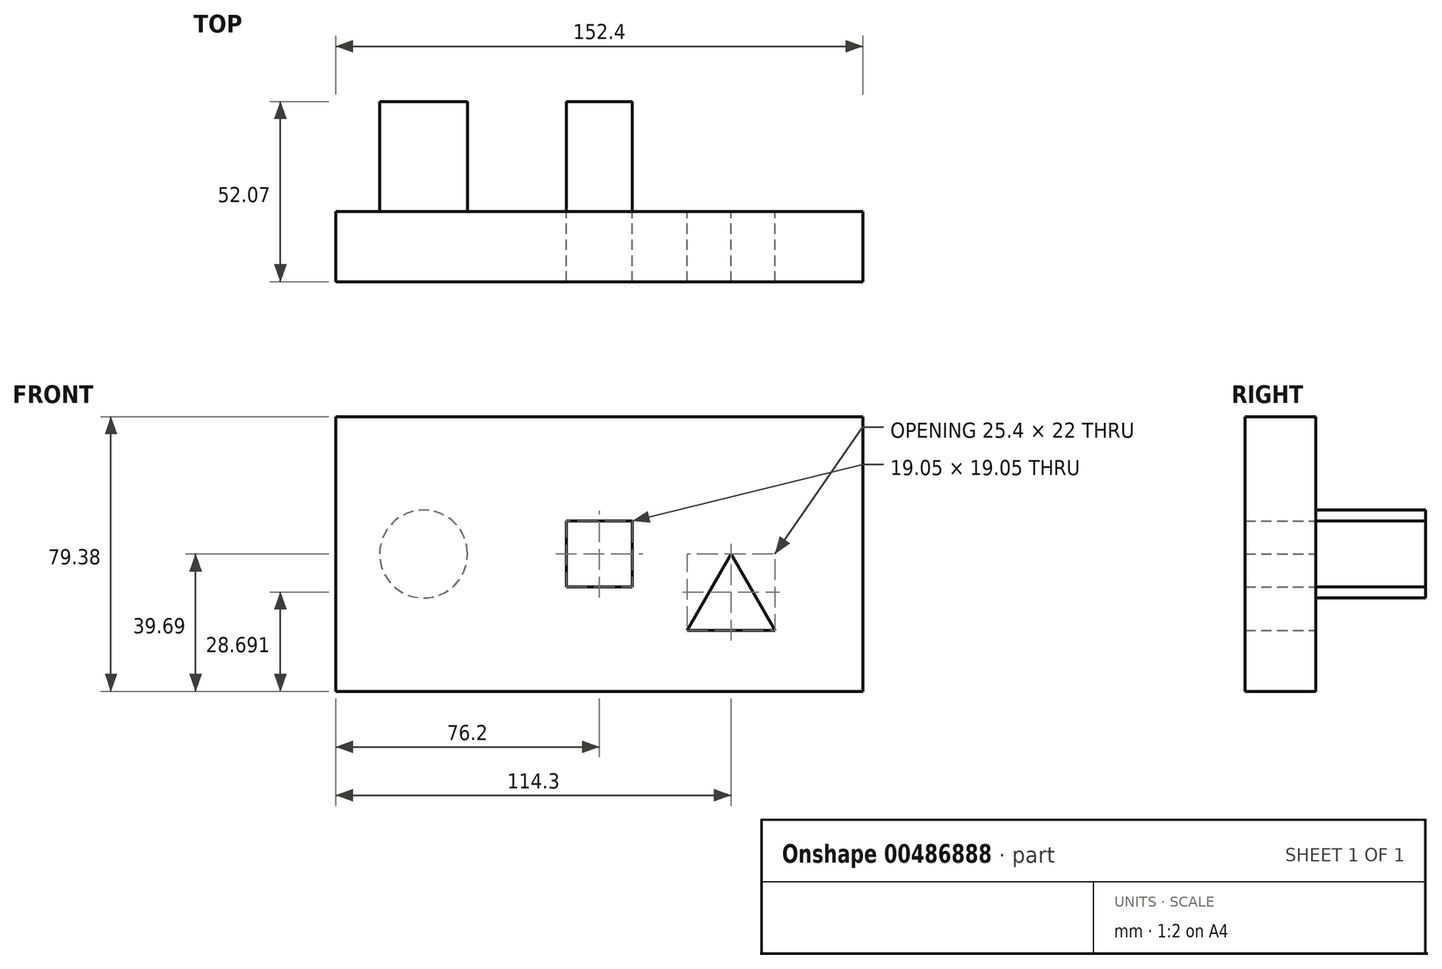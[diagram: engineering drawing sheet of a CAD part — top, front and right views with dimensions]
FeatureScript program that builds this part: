
annotation { "Feature Type Name" : "Feature", "Feature Type Description" : "" }
export const myFeature = defineFeature(function(context is Context, id is Id, definition is map)
    precondition{}
    {
        {
            var Q0;
            Q0=qCreatedBy(makeId("Front.planeOp"),FACE);
            var sketch = newSketch(context, id + "F0", { "sketchPlane" : qUnion([Q0])});
            skLineSegment(sketch, "E0.bottom", {"start": v(44.45, 39.69) * mm, "end": v(-107.95, 39.69) * mm});
            skLineSegment(sketch, "E0.top", {"start": v(44.45, -39.69) * mm, "end": v(-107.95, -39.69) * mm});
            skLineSegment(sketch, "E0.left", {"start": v(44.45, 39.69) * mm, "end": v(44.45, -39.69) * mm});
            skLineSegment(sketch, "E0.right", {"start": v(-107.95, 39.69) * mm, "end": v(-107.95, -39.69) * mm});
            skLineSegment(sketch, "E1", {"start": v(6.35, 0) * mm, "end": v(-6.35, -22) * mm});
            skLineSegment(sketch, "E2", {"start": v(-6.35, -22) * mm, "end": v(19.05, -22) * mm});
            skLineSegment(sketch, "E3", {"start": v(19.05, -22) * mm, "end": v(6.35, 0) * mm});
            skLineSegment(sketch, "E4.bottom", {"start": v(-22.22, 9.53) * mm, "end": v(-41.27, 9.53) * mm});
            skLineSegment(sketch, "E4.top", {"start": v(-22.23, -9.53) * mm, "end": v(-41.27, -9.52) * mm});
            skLineSegment(sketch, "E4.left", {"start": v(-22.22, 9.53) * mm, "end": v(-22.23, -9.53) * mm});
            skLineSegment(sketch, "E4.right", {"start": v(-41.27, 9.53) * mm, "end": v(-41.27, -9.53) * mm});
            skPoint(sketch, "E4.middle", {"position": v(-31.75, 0) * mm});
            skCircle(sketch, "E5", {"center": v(-82.55, 0) * mm, "radius": 12.7 * mm});
            skSolve(sketch);
        }
        {
            var Q0;
            Q0=makeQuery(id+"F0.imprint","IMPRINT",FACE,{"disambiguationData":[TD([[makeQuery(id+"F0.imprint","IMPRINT",EDGE,{"derivedFrom":sQuery(id+"F0.wireOp",EDGE,"E0.bottom")}),1.0]])]});
            extrude(context, id + "F1", {"entities" : qUnion([Q0]), "depth" : 20.32 * mm});
        }
        {
            var Q0;
            Q0=makeQuery(id+"F0.imprint","IMPRINT",FACE,{"disambiguationData":[TD([[makeQuery(id+"F0.imprint","IMPRINT",EDGE,{"derivedFrom":sQuery(id+"F0.wireOp",EDGE,"E4.bottom")}),1.0]])]});
            extrude(context, id + "F2", {"entities" : qUnion([Q0]), "operationType" : NewBodyOperationType.ADD, "oppositeDirection" : true, "depth" : 31.75 * mm});
        }
        {
            var Q0;
            Q0=makeQuery(id+"F0.imprint","IMPRINT",FACE,{"disambiguationData":[TD([[makeQuery(id+"F0.imprint","IMPRINT",EDGE,{"derivedFrom":sQuery(id+"F0.wireOp",EDGE,"E5")}),1.0]])]});
            extrude(context, id + "F3", {"entities" : qUnion([Q0]), "operationType" : NewBodyOperationType.ADD, "depth" : 20.32 * mm});
        }
        {
            var Q0;
            Q0=makeQuery(id+"F0.imprint","IMPRINT",FACE,{"disambiguationData":[TD([[makeQuery(id+"F0.imprint","IMPRINT",EDGE,{"derivedFrom":sQuery(id+"F0.wireOp",EDGE,"E5")}),1.0]])]});
            extrude(context, id + "F4", {"entities" : qUnion([Q0]), "operationType" : NewBodyOperationType.ADD, "oppositeDirection" : true, "depth" : 31.75 * mm});
        }
    });
